# Revit family: P210059AX-002_NGD4655EW
name_source: partatom
category: Specialty Equipment
units: mm (PartAtom-declared; Revit-internal decimal feet)

## family parameters
Always vertical = Yes
Cut with Voids When Loaded = No
Enable Cutting in Views = No
Maintain Annotation Orientation = No
Part Type = Normal
Room Calculation Point = No
Round Connector Dimension = Use Diameter
Shared = No
Work Plane-Based = No

## types (1)
- NGD4655EW
    Amps = 30 A
    Back Panel Material = ARCAT - Metal - Aluminum
    Body Material = ARCAT - Metal - Steel - White
    Clearance Material = ARCAT - Clearance
    Default Elevation = 0"
    Depth = 28 1/4"
    Description = 6.5 cu. ft. Gas Dryer with Wrinkle Prevent Option
Sécheuse au gaz à chargement vertical de 6.5 pi cu avec contrôle de séchage automatique
    Dimension Guide = https://whirlpool.com
https://whirlpool.com
    Family Name = Gas top load dryer
    Feature 1 = Automatic Dryness Control
Contrôle de séchage  automatique
    Feature 2 = Wrinkle Prevent Option
Option antifroissement Wrinkle PreventTM
    Feature 3 = 6.5 Cu. Ft. Capacity
Capacité de 6,5 pi³
    Handle Material = ARCAT - Metal - Steel - White
    Height = 44"
    Hinges Material = ARCAT - Metal - Steel - Stainless
    Installation-Fabrication = https://access.whirlpool.com Instruction&sku=NGD4655EW&language=EN
http://access.whirlpool.com Instruction&sku=NGD4655EW&language=FR
    Knob Material = ARCAT - Plastic - White
    Leg Material = ARCAT - Metal - Steel - Stainless
    Manufacturer = Amana
    Model = NGD4655EW
    Voltage = 0 V
    Width = 29"

## geometry (parser evidence)
native form markers: Sweep x4
no freeform markers — native parametric forms only
